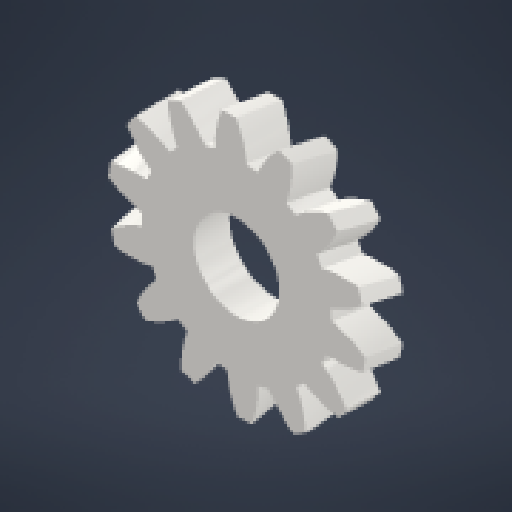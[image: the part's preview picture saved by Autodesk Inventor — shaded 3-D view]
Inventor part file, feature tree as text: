
AUTODESK INVENTOR PART (.ipt)
format: ipt  version: 2024.2 (Build 282272000, 272)  size: 354,304 bytes
history: native  units: mm (DEFAULTED — no unit token found)
features: extrude x3, plane x3, other x3, sketch x3
ambient origin geometry x8: Origin, YZ Plane, XZ Plane, XY Plane, X Axis, Y Axis, Z Axis, Center Point
bodies: Solid1 (feature_tree)
feature tree (12):
  extrude  "Extrusion1"  Depth=6.35mm TaperAngle=0.0deg
  plane  "Work Plane1"
  plane  "Work Plane2"
  plane  "Work Plane3"
  other  "Spur Gear"
  extrude  "Extrusion2"  Depth=76.2mm TaperAngle=0.0deg
  extrude  "Extrusion3"  TaperAngle=0.0deg  [1 undecoded]
  sketch  "Sketch1"  dims[d0=42.577228mm d1=6.35mm d2=0.0mm]
  other  "Srf1"
  sketch  "Sketch3"  dims[d3=36.10857mm d4=76.2mm d5=0.0mm]
  sketch  "Sketch4"  dims[d6=0.0mm d7=2.243995mm d9=0.0mm d14=0.0mm d15=35.513307mm d16=0.0mm d17=0.0mm d18=0.0mm d19=35.513307mm d20=15.0mm d21=1.0mm d22=0.0mm d23=14.0mm d24=0.0mm d25=0.0mm]
  other  "Pitch Diameter"
note: 1 required parameter value undecoded (feature->parameter linkage not recoverable at this tier; creation-order binding heuristic only, values carry confidence <= 0.55)
